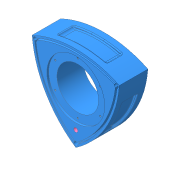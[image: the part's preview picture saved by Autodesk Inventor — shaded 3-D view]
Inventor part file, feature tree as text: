
AUTODESK INVENTOR PART (.ipt)
format: ipt  version: 2016 (Build 200138000, 138)  size: 591,360 bytes
history: native  units: in
note: dims shown in document units (in); Inventor stores cm internally (conversion verified against a paired STEP export)
features: thread x7
ambient origin geometry x8: Origin, YZ Plane, XZ Plane, XY Plane, X Axis, Y Axis, Z Axis, Center Point
bodies: Solid2 (feature_tree), Solid1 (feature_tree)
feature tree (7):
  thread  "Thread1"  [1 undecoded]
  thread  "Thread2"  [1 undecoded]
  thread  "Thread3"  [1 undecoded]
  thread  "Thread4"  [1 undecoded]
  thread  "Thread5"  [1 undecoded]
  thread  "Thread6"  [1 undecoded]
  thread  "Thread7"  [1 undecoded]
note: 7 required parameter values undecoded (feature->parameter linkage not recoverable at this tier; creation-order binding heuristic only, values carry confidence <= 0.55)
